# Revit family: Bench_Locker-Bradley_Corp-Lenox_5_Cubby_Bench
name_source: partatom
category: Specialty Equipment
units: mm (PartAtom-declared; Revit-internal decimal feet)

## family parameters
Always vertical = Yes
Cut with Voids When Loaded = No
OmniClass Number = 23.40.00.00
OmniClass Title = Equipment and Furnishings
Part Type = Normal
Room Calculation Point = No
Round Connector Dimension = Use Diameter
Shared = No
Work Plane-Based = No

## types (1)
- 60" Long - 5 Cubby Locker
    ADA Compliant = No
    Assembly Code = C1030310
    Default Elevation = 0"
    Description = Solid Plastic Cubby Bench & Lockers
    Height = 19 3/4"
    Manufacturer = Bradley Corporation
    MasterFormat Number = 10 51 26
    MasterFormat Title = Plastic Lockers
    Material Note = Other colors available - see www.bradleycorp.com
    Model = Lenox Cubby Bench Lockers
    OmniClass Table 21 Number = 21-03 10 90 70
    OmniClass Table 21 Title = Storage Specialties
    OmniClass Table 23 Number = 23-21 15 15
    OmniClass Table 23 Title = Clothing Lockers
    Product Page URL = https://www.bradleycorp.com
    Product Tech Data URL - English = https://www.bradleycorp.com
    Specifications URL = https://www.bradleycorp.com
    Tiers = 2
    URL = http://www.bradleycorp.com
    Version = 2023-08-18
    Warranty Information = 20 years

## geometry (parser evidence)
native form markers: Sweep x2
no freeform markers — native parametric forms only
